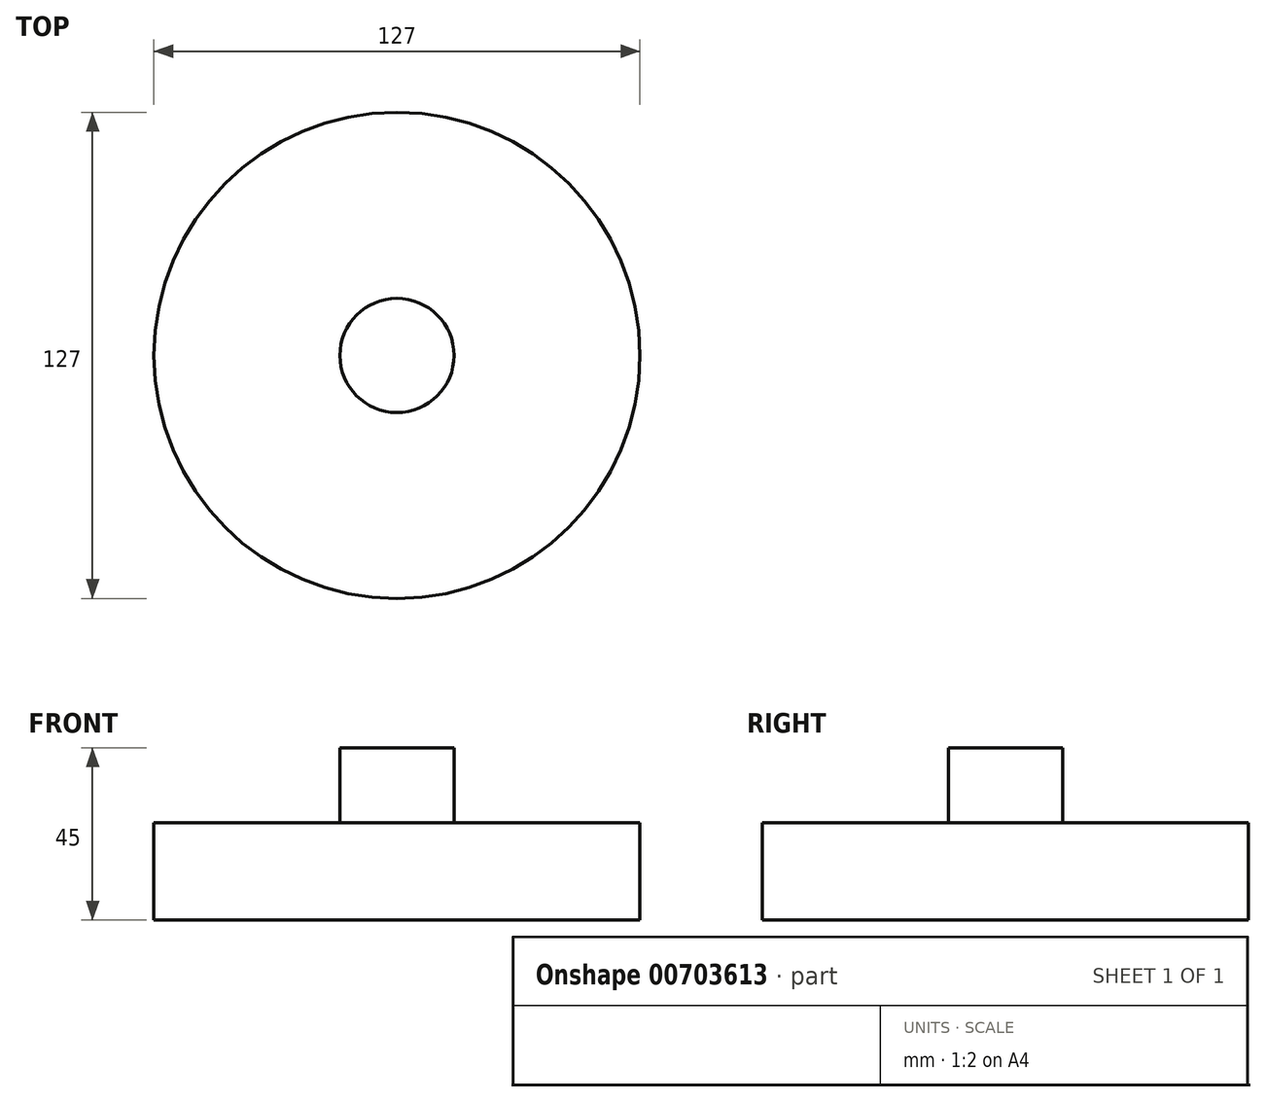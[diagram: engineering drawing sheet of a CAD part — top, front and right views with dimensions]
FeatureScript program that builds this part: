
annotation { "Feature Type Name" : "Feature", "Feature Type Description" : "" }
export const myFeature = defineFeature(function(context is Context, id is Id, definition is map)
    precondition{}
    {
        {
            var Q0;
            Q0=qCreatedBy(makeId("Top.planeOp"),FACE);
            var sketch = newSketch(context, id + "F0", { "sketchPlane" : qUnion([Q0])});
            skCircle(sketch, "E0", {"center": v(0, 0) * mm, "radius": 63.5 * mm});
            skCircle(sketch, "E1", {"center": v(0, 0) * mm, "radius": 3.94 * mm});
            skCircle(sketch, "E2", {"center": v(0, 0) * mm, "radius": 14.14 * mm});
            skSolve(sketch);
        }
        {
            var Q0;
            Q0=makeQuery(id+"F0.imprint","IMPRINT",FACE,{"disambiguationData":[TD([[makeQuery(id+"F0.imprint","IMPRINT",EDGE,{"derivedFrom":sQuery(id+"F0.wireOp",EDGE,"E0")}),1.0]])]});
            extrude(context, id + "F1", {"entities" : qUnion([Q0]), "depth" : 25.4 * mm, "offsetDistance" : 25.4 * mm});
        }
        {
            var Q0;
            Q0=qCreatedBy(makeId("Top.planeOp"),FACE);
            var sketch = newSketch(context, id + "F2", { "sketchPlane" : qUnion([Q0])});
            skCircle(sketch, "E3", {"center": v(0, 0) * mm, "radius": 14.9 * mm});
            skSolve(sketch);
        }
        {
            var Q0;
            Q0 = qSketchRegion(id + "F2", true);
            extrude(context, id + "F3", {"entities" : qUnion([Q0]), "operationType" : NewBodyOperationType.ADD, "depth" : 45 * mm, "offsetDistance" : 25 * mm});
        }
    });
